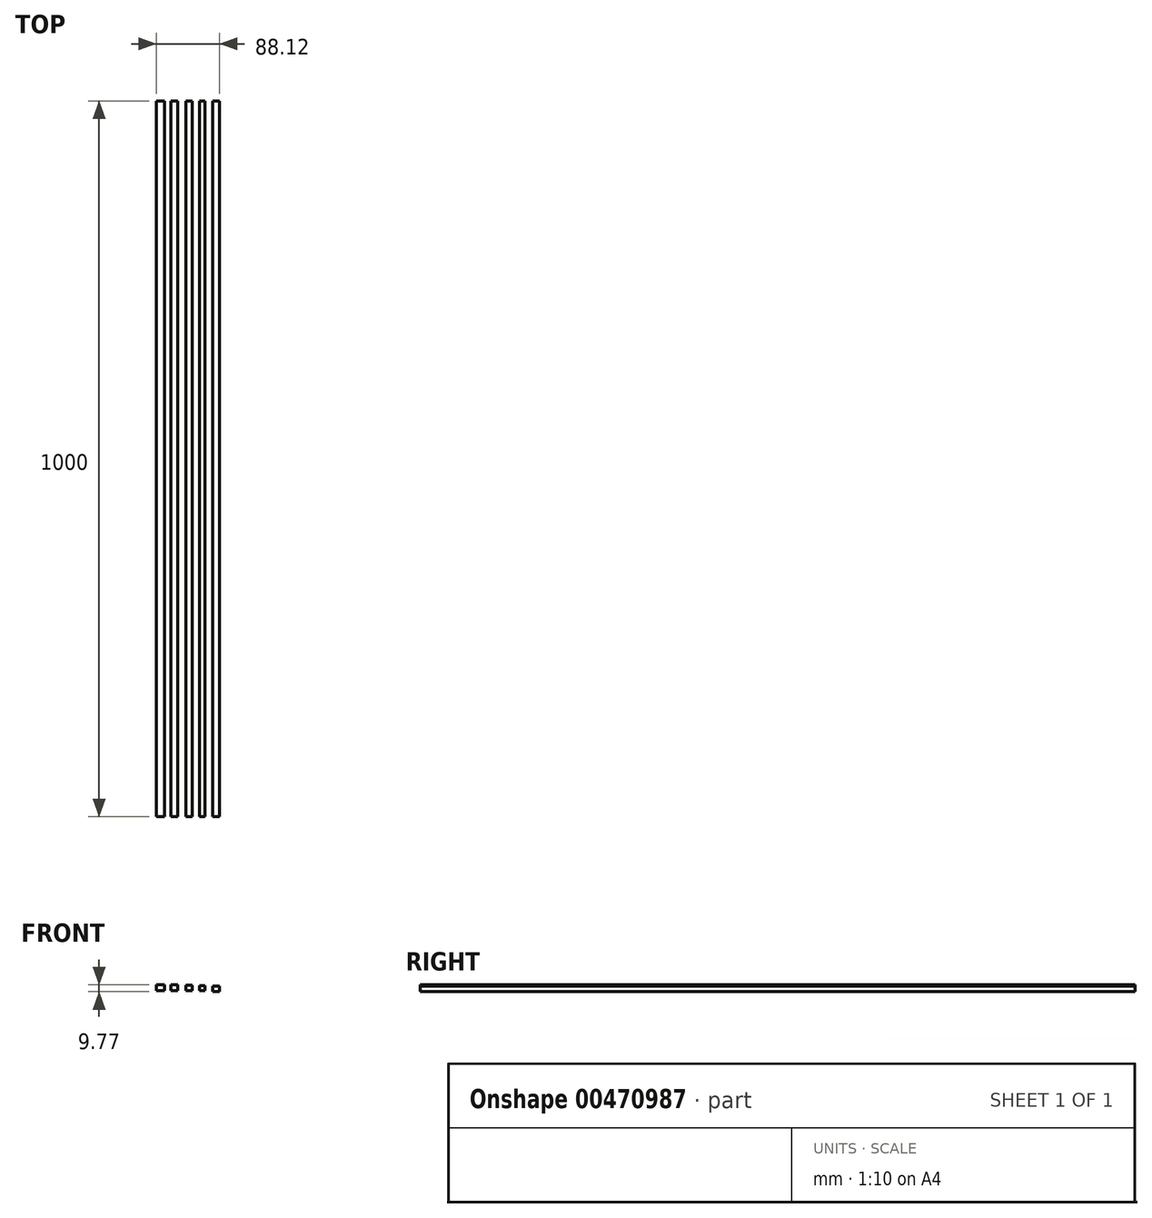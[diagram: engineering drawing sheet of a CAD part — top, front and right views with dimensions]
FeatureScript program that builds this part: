
annotation { "Feature Type Name" : "Feature", "Feature Type Description" : "" }
export const myFeature = defineFeature(function(context is Context, id is Id, definition is map)
    precondition{}
    {
        {
            var Q0;
            Q0=qCreatedBy(makeId("Front.planeOp"),FACE);
            var sketch = newSketch(context, id + "F0", { "sketchPlane" : qUnion([Q0])});
            skLineSegment(sketch, "E0.bottom", {"start": v(-49.96, 8.3) * mm, "end": v(-38.53, 8.3) * mm});
            skLineSegment(sketch, "E0.top", {"start": v(-49.96, 0) * mm, "end": v(-38.53, 0) * mm});
            skLineSegment(sketch, "E0.left", {"start": v(-49.96, 8.3) * mm, "end": v(-49.96, 0) * mm});
            skLineSegment(sketch, "E0.right", {"start": v(-38.53, 8.3) * mm, "end": v(-38.53, 0) * mm});
            skLineSegment(sketch, "E1.bottom", {"start": v(-29.87, 8.11) * mm, "end": v(-19.91, 8.11) * mm});
            skLineSegment(sketch, "E1.top", {"start": v(-29.87, 0) * mm, "end": v(-19.91, 0) * mm});
            skLineSegment(sketch, "E1.left", {"start": v(-29.87, 8.11) * mm, "end": v(-29.87, 0) * mm});
            skLineSegment(sketch, "E1.right", {"start": v(-19.91, 8.11) * mm, "end": v(-19.91, 0) * mm});
            skLineSegment(sketch, "E2.bottom", {"start": v(-8.66, 7.56) * mm, "end": v(0, 7.56) * mm});
            skLineSegment(sketch, "E2.top", {"start": v(-8.66, 0) * mm, "end": v(0, 0) * mm});
            skLineSegment(sketch, "E2.left", {"start": v(-8.66, 7.56) * mm, "end": v(-8.66, 0) * mm});
            skLineSegment(sketch, "E2.right", {"start": v(0, 7.56) * mm, "end": v(0, 0) * mm});
            skLineSegment(sketch, "E3.bottom", {"start": v(10.14, 6.82) * mm, "end": v(18.07, 6.82) * mm});
            skLineSegment(sketch, "E3.top", {"start": v(10.14, 0) * mm, "end": v(18.07, 0) * mm});
            skLineSegment(sketch, "E3.left", {"start": v(10.14, 6.82) * mm, "end": v(10.14, 0) * mm});
            skLineSegment(sketch, "E3.right", {"start": v(18.07, 6.82) * mm, "end": v(18.07, 0) * mm});
            skLineSegment(sketch, "E4.bottom", {"start": v(28.76, 6.27) * mm, "end": v(38.16, 6.27) * mm});
            skLineSegment(sketch, "E4.top", {"start": v(28.76, -1.47) * mm, "end": v(38.16, -1.47) * mm});
            skLineSegment(sketch, "E4.left", {"start": v(28.76, 6.27) * mm, "end": v(28.76, -1.47) * mm});
            skLineSegment(sketch, "E4.right", {"start": v(38.16, 6.27) * mm, "end": v(38.16, -1.47) * mm});
            skSolve(sketch);
        }
        {
            var Q0;
            Q0=makeQuery(id+"F0.imprint","IMPRINT",FACE,{"disambiguationData":[TD([[makeQuery(id+"F0.imprint","IMPRINT",EDGE,{"derivedFrom":sQuery(id+"F0.wireOp",EDGE,"E0.bottom")}),-1.0]])]});
            var Q1;
            Q1=makeQuery(id+"F0.imprint","IMPRINT",FACE,{"disambiguationData":[TD([[makeQuery(id+"F0.imprint","IMPRINT",EDGE,{"derivedFrom":sQuery(id+"F0.wireOp",EDGE,"E1.bottom")}),-1.0]])]});
            var Q2;
            Q2=makeQuery(id+"F0.imprint","IMPRINT",FACE,{"disambiguationData":[TD([[makeQuery(id+"F0.imprint","IMPRINT",EDGE,{"derivedFrom":sQuery(id+"F0.wireOp",EDGE,"E2.bottom")}),-1.0]])]});
            var Q3;
            Q3=makeQuery(id+"F0.imprint","IMPRINT",FACE,{"disambiguationData":[TD([[makeQuery(id+"F0.imprint","IMPRINT",EDGE,{"derivedFrom":sQuery(id+"F0.wireOp",EDGE,"E3.bottom")}),-1.0]])]});
            var Q4;
            Q4=makeQuery(id+"F0.imprint","IMPRINT",FACE,{"disambiguationData":[TD([[makeQuery(id+"F0.imprint","IMPRINT",EDGE,{"derivedFrom":sQuery(id+"F0.wireOp",EDGE,"E4.bottom")}),-1.0]])]});
            extrude(context, id + "F1", {"entities" : qUnion([Q0, Q1, Q2, Q3, Q4]), "depth" : 1000 * mm});
        }
    });
